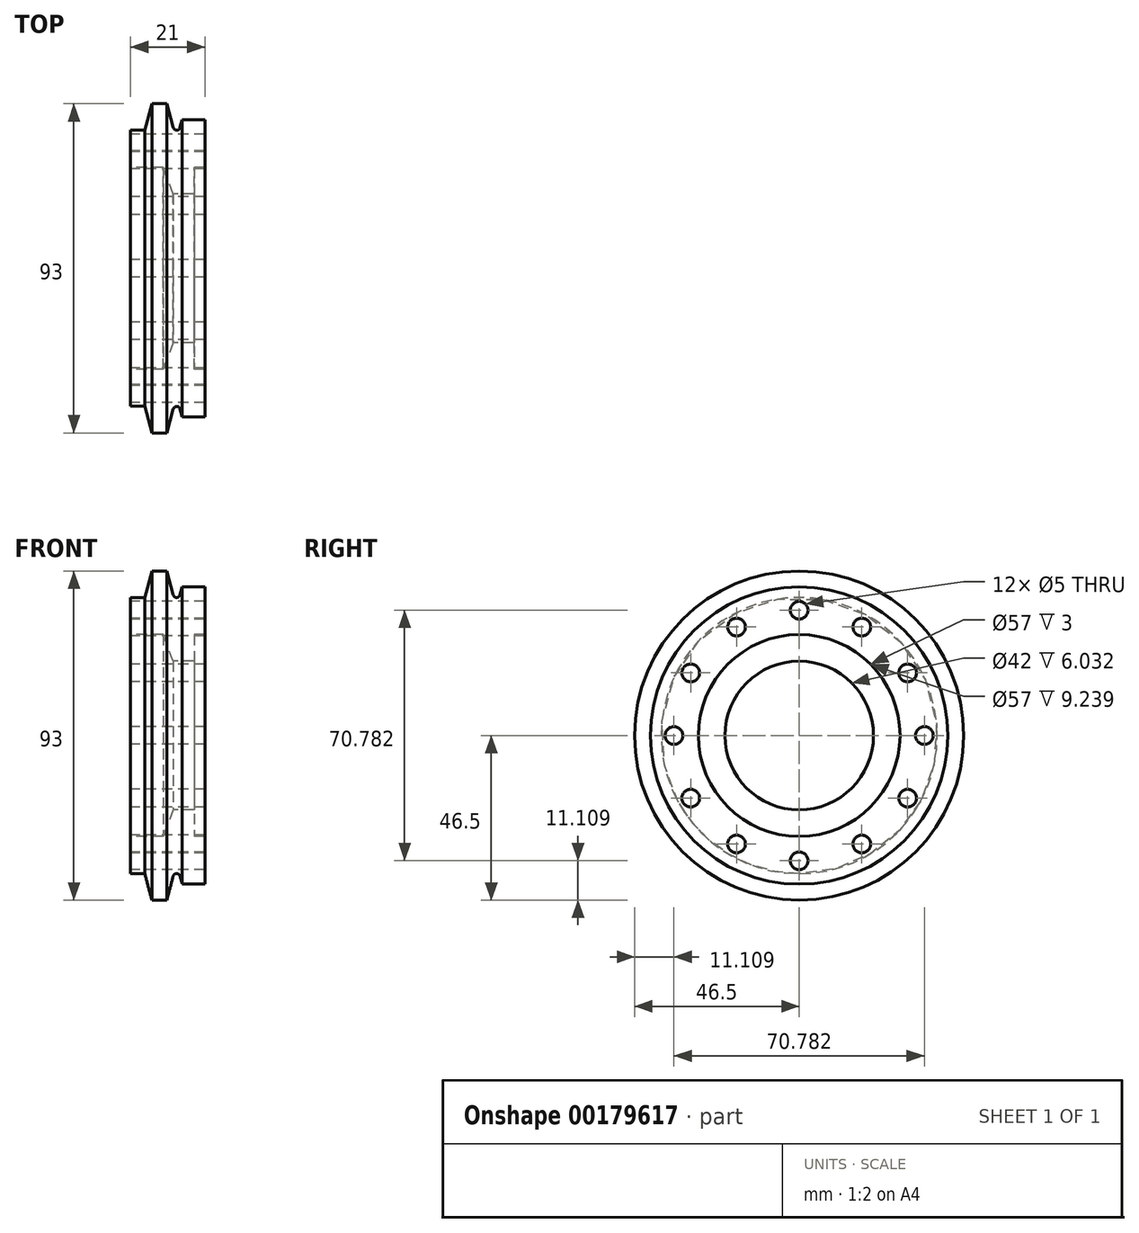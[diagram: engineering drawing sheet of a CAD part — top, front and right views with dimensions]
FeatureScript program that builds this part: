
annotation { "Feature Type Name" : "Feature", "Feature Type Description" : "" }
export const myFeature = defineFeature(function(context is Context, id is Id, definition is map)
    precondition{}
    {
        {
            var Q0;
            Q0=qCreatedBy(makeId("Front.planeOp"),FACE);
            var sketch = newSketch(context, id + "F0", { "sketchPlane" : qUnion([Q0])});
            skLineSegment(sketch, "E0", {"start": v(0, 0) * mm, "end": v(0, 39) * mm});
            skLineSegment(sketch, "E1", {"start": v(0, 39) * mm, "end": v(4, 39) * mm});
            skLineSegment(sketch, "E2", {"start": v(14.57, 42) * mm, "end": v(21, 42) * mm});
            skLineSegment(sketch, "E3", {"start": v(21, 42) * mm, "end": v(21, 0) * mm});
            skLineSegment(sketch, "E4", {"start": v(21, 0) * mm, "end": v(0, 0) * mm});
            skLineSegment(sketch, "E5", {"start": v(6, 46.5) * mm, "end": v(10.22, 46.5) * mm});
            skLineSegment(sketch, "E6", {"start": v(13.97, 39.74) * mm, "end": v(14.57, 42) * mm});
            skLineSegment(sketch, "E7", {"start": v(10.22, 46.5) * mm, "end": v(12.03, 39.74) * mm});
            skPoint(sketch, "E8.visualSharp", {"position": v(13, 36.14) * mm});
            skArc(sketch, "E8.filletArc", {"start": v(12.03, 39.74) * mm, "mid": v(13, 39) * mm, "end": v(13.97, 39.74) * mm});
            skLineSegment(sketch, "E9", {"start": v(6, 46.5) * mm, "end": v(4, 39) * mm});
            skSolve(sketch);
        }
        {
            var Q0;
            Q0 = qSketchRegion(id + "F0", true);
            var Q1;
            Q1=sQuery(id+"F0.wireOp",EDGE,"E4");
            revolve(context, id + "F1", {"entities" : qUnion([Q0]), "axis" : qUnion([Q1]), "revolveType" : RevolveType.FULL});
        }
        {
            var Q0;
            Q0=qCreatedBy(makeId("Front.planeOp"),FACE);
            var sketch = newSketch(context, id + "F2", { "sketchPlane" : qUnion([Q0])});
            skLineSegment(sketch, "E10", {"start": v(0, 0) * mm, "end": v(0, 28.5) * mm});
            skLineSegment(sketch, "E11", {"start": v(0, 28.5) * mm, "end": v(9.24, 28.5) * mm});
            skLineSegment(sketch, "E12", {"start": v(11.97, 21) * mm, "end": v(18, 21) * mm});
            skLineSegment(sketch, "E13", {"start": v(18, 21) * mm, "end": v(18, 28.5) * mm});
            skLineSegment(sketch, "E14", {"start": v(18, 28.5) * mm, "end": v(24, 28.5) * mm});
            skLineSegment(sketch, "E15", {"start": v(24, 28.5) * mm, "end": v(24, 0) * mm});
            skLineSegment(sketch, "E16", {"start": v(24, 0) * mm, "end": v(0, 0) * mm});
            skLineSegment(sketch, "E17", {"start": v(9.24, 28.5) * mm, "end": v(11.97, 21) * mm});
            skSolve(sketch);
        }
        {
            var Q0;
            Q0 = qSketchRegion(id + "F2", true);
            var Q1;
            Q1=sQuery(id+"F2.wireOp",EDGE,"E16");
            revolve(context, id + "F3", {"operationType" : NewBodyOperationType.REMOVE, "entities" : qUnion([Q0]), "axis" : qUnion([Q1]), "revolveType" : RevolveType.FULL, "oppositeDirection" : true});
        }
        {
            var Q0;
            Q0=qCreatedBy(makeId("Right.planeOp"),FACE);
            var sketch = newSketch(context, id + "F4", { "sketchPlane" : qUnion([Q0])});
            skCircle(sketch, "E18", {"center": v(-35.4, 0) * mm, "radius": 2.5 * mm});
            skCircle(sketch, "E19.1.0", {"center": v(-30.65, -17.7) * mm, "radius": 2.5 * mm});
            skCircle(sketch, "E19.2.0", {"center": v(-17.7, -30.65) * mm, "radius": 2.5 * mm});
            skCircle(sketch, "E19.3.0", {"center": v(0, -35.4) * mm, "radius": 2.5 * mm});
            skCircle(sketch, "E19.4.0", {"center": v(17.7, -30.65) * mm, "radius": 2.5 * mm});
            skCircle(sketch, "E19.5.0", {"center": v(30.65, -17.7) * mm, "radius": 2.5 * mm});
            skCircle(sketch, "E19.6.0", {"center": v(35.4, 0) * mm, "radius": 2.5 * mm});
            skCircle(sketch, "E19.7.0", {"center": v(30.65, 17.7) * mm, "radius": 2.5 * mm});
            skCircle(sketch, "E19.8.0", {"center": v(17.7, 30.65) * mm, "radius": 2.5 * mm});
            skCircle(sketch, "E19.9.0", {"center": v(0, 35.4) * mm, "radius": 2.5 * mm});
            skCircle(sketch, "E19.10.0", {"center": v(-17.7, 30.65) * mm, "radius": 2.5 * mm});
            skCircle(sketch, "E19.11.0", {"center": v(-30.65, 17.7) * mm, "radius": 2.5 * mm});
            skPoint(sketch, "E19.center", {"position": v(0, 0) * mm});
            skLineSegment(sketch, "E19.anchor1", {"start": v(0, 0) * mm, "end": v(-35.4, 0) * mm, "construction": true});
            skLineSegment(sketch, "E19.anchor2", {"start": v(0, 0) * mm, "end": v(-30.65, 17.7) * mm, "construction": true});
            skSolve(sketch);
        }
        {
            var Q0;
            Q0 = qSketchRegion(id + "F4", true);
            extrude(context, id + "F5", {"entities" : qUnion([Q0]), "operationType" : NewBodyOperationType.REMOVE, "depth" : 25 * mm});
        }
    });
